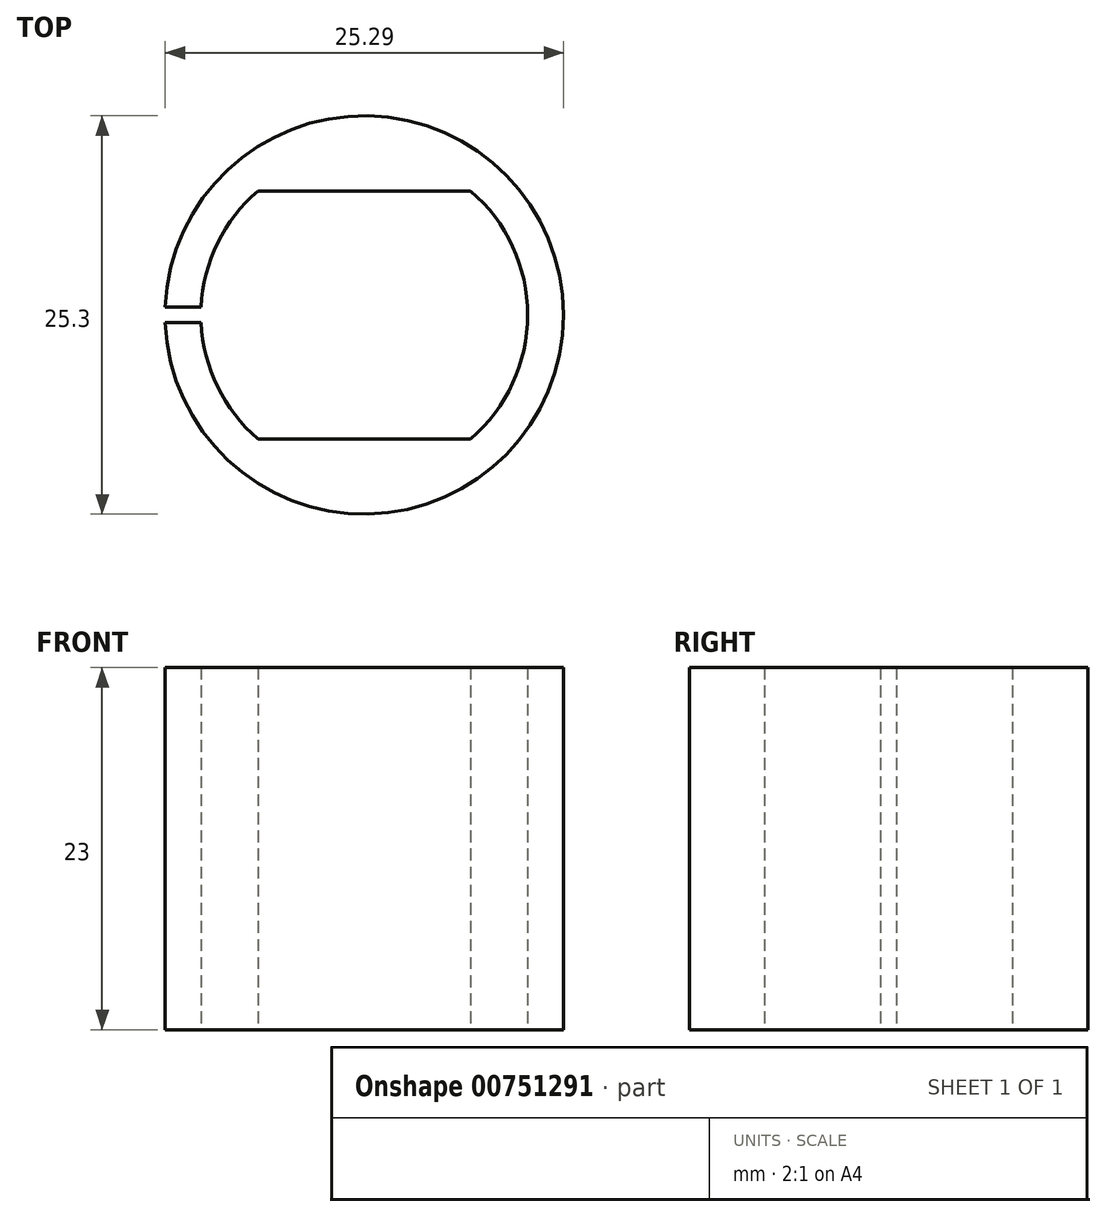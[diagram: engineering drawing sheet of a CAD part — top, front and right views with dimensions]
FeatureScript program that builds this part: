
annotation { "Feature Type Name" : "Feature", "Feature Type Description" : "" }
export const myFeature = defineFeature(function(context is Context, id is Id, definition is map)
    precondition{}
    {
        {
            var Q0;
            Q0=qCreatedBy(makeId("Top.planeOp"),FACE);
            var sketch = newSketch(context, id + "F0", { "sketchPlane" : qUnion([Q0])});
            skCircle(sketch, "E0", {"center": v(0, 0) * mm, "radius": 12.65 * mm});
            skArc(sketch, "E1", {"start": v(-6.75, 7.87) * mm, "mid": v(-10.37, 0) * mm, "end": v(-6.75, -7.87) * mm});
            skLineSegment(sketch, "E2", {"start": v(-6.75, 7.88) * mm, "end": v(6.75, 7.88) * mm});
            skLineSegment(sketch, "E3.MirrorCS", {"start": v(-6.75, -7.88) * mm, "end": v(6.75, -7.88) * mm});
            skArc(sketch, "E4.trimOffspring", {"start": v(6.75, -7.88) * mm, "mid": v(10.38, 0) * mm, "end": v(6.75, 7.88) * mm});
            skLineSegment(sketch, "E5", {"start": v(-12.64, 0.5) * mm, "end": v(-10.36, 0.5) * mm});
            skLineSegment(sketch, "E6", {"start": v(-12.64, -0.5) * mm, "end": v(-10.36, -0.5) * mm});
            skSolve(sketch);
        }
        {
            var Q0;
            {var subQ0=sQuery(id+"F0.wireOp",EDGE,"E2");Q0=makeQuery(id+"F0.imprint","IMPRINT",FACE,{"disambiguationData":[TD([[makeQuery(id+"F0.imprint","IMPRINT",EDGE,{"derivedFrom":subQ0}),1.0]])]});}
            extrude(context, id + "F1", {"entities" : qUnion([Q0]), "depth" : 23 * mm, "offsetDistance" : 25 * mm});
        }
    });
